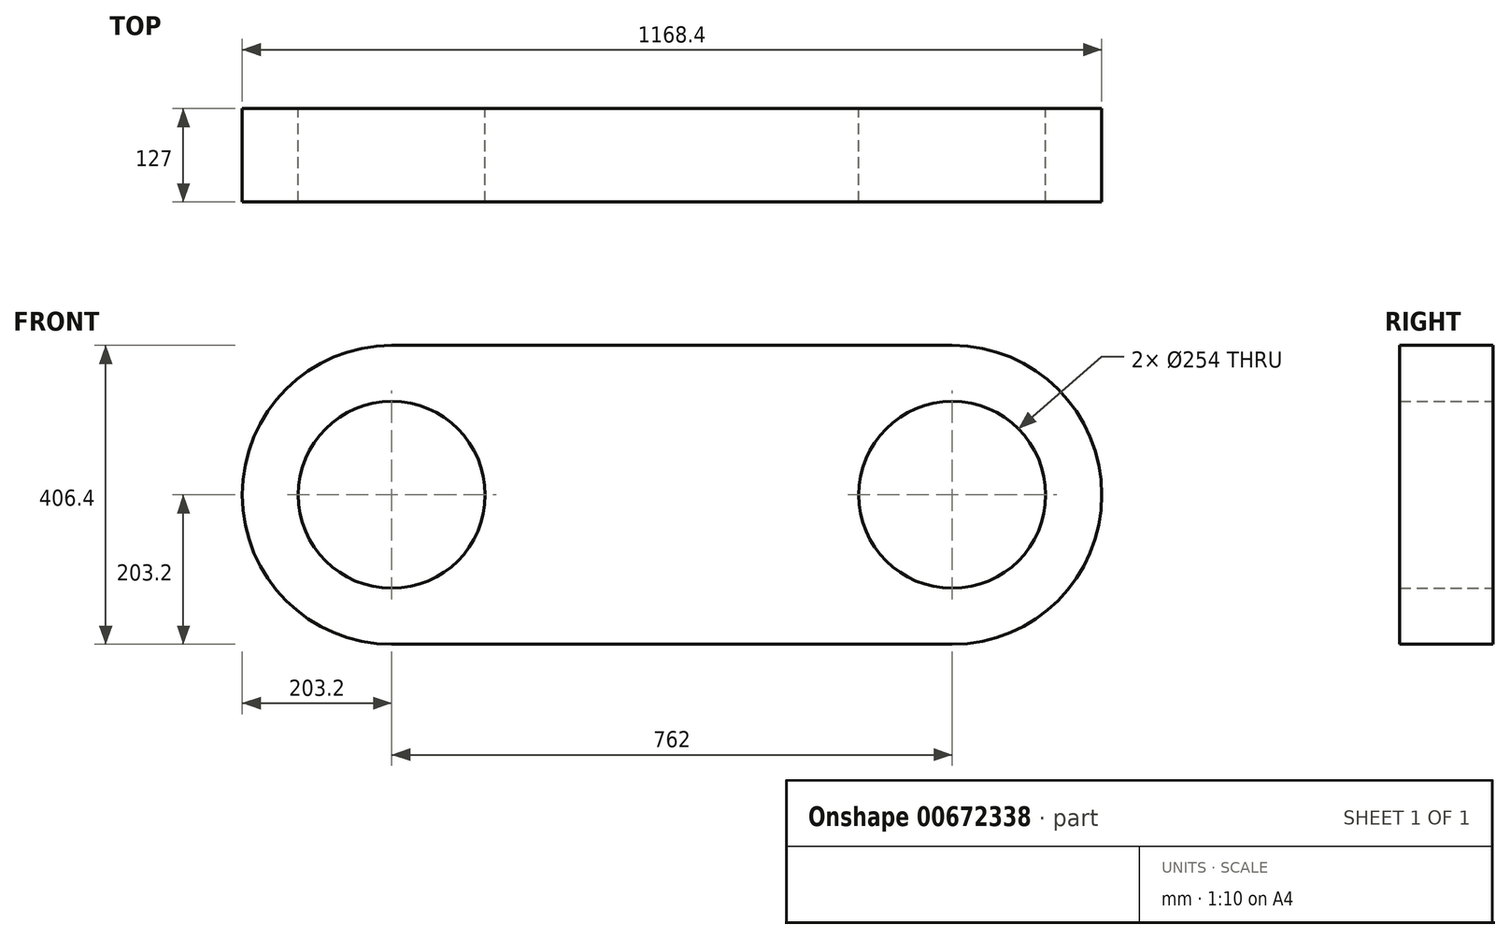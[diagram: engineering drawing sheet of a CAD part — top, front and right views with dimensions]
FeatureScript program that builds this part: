
annotation { "Feature Type Name" : "Feature", "Feature Type Description" : "" }
export const myFeature = defineFeature(function(context is Context, id is Id, definition is map)
    precondition{}
    {
        {
            var Q0;
            Q0=qCreatedBy(makeId("Front.planeOp"),FACE);
            var sketch = newSketch(context, id + "F0", { "sketchPlane" : qUnion([Q0])});
            skLineSegment(sketch, "E0.bottom", {"start": v(-381, 203.2) * mm, "end": v(381, 203.2) * mm});
            skLineSegment(sketch, "E0.top", {"start": v(-381, -203.2) * mm, "end": v(381, -203.2) * mm});
            skArc(sketch, "E1", {"start": v(-381, 203.2) * mm, "mid": v(-584.2, 0) * mm, "end": v(-381, -203.2) * mm});
            skArc(sketch, "E2", {"start": v(381, -203.2) * mm, "mid": v(584.2, 0) * mm, "end": v(381, 203.2) * mm});
            skCircle(sketch, "E3", {"center": v(-381, 0) * mm, "radius": 127 * mm});
            skCircle(sketch, "E4", {"center": v(381, 0) * mm, "radius": 127 * mm});
            skSolve(sketch);
        }
        {
            var Q0;
            Q0 = qSketchRegion(id + "F0", true);
            extrude(context, id + "F1", {"entities" : qUnion([Q0]), "depth" : 127 * mm, "offsetDistance" : 25.4 * mm});
        }
    });
